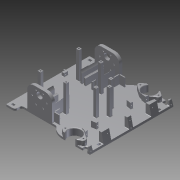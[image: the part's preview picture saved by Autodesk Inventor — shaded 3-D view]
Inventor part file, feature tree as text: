
AUTODESK INVENTOR PART (.ipt)
format: ipt  version: 2011 SP2 (Build 150309200, 309)  size: 1,402,880 bytes
history: native  units: mm
features: extrude x35, sketch x21, projected_geometry x14, fillet x12, mirror x2, plane x1, chamfer x1, hole x1
ambient origin geometry x8: Origin, YZ Plane, XZ Plane, XY Plane, X Axis, Y Axis, Z Axis, Center Point
feature tree (87):
  sketch  "Sketch1"  dims[d0=200.0mm d1=200.0mm]
  extrude  "Extrusion3"  Depth=200.0mm
  extrude  "Extrusion4"  Depth=10.5mm
  extrude  "Extrusion5"  Depth=6.5mm
  extrude  "Extrusion6"  Depth=53.3mm
  extrude  "Extrusion7"  Depth=26.65mm
  sketch  "Sketch4"  dims[d6=6.5mm d8=53.3mm]
  extrude  "Extrusion8"  Depth=5.0mm
  extrude  "Extrusion9"  Depth=5.0mm
  extrude  "Extrusion10"  Depth=4.4mm
  plane  "Work Plane1"
  mirror  "Mirror1"
  sketch  "Sketch9"  dims[d9=53.3mm d10=26.65mm]
  sketch  "Sketch10"  dims[d11=26.65mm d13=5.0mm]
  extrude  "Extrusion16"  Depth=8.0mm
  extrude  "Extrusion17"  Depth=8.0mm
  extrude  "Extrusion18"  Depth=60.0mm
  extrude  "Extrusion19"  Depth=39.0mm
  extrude  "Extrusion20"  Depth=3.65mm
  extrude  "Extrusion21"  Depth=1.5mm
  extrude  "Extrusion22"  Depth=6.6mm
  sketch  "Sketch13"  dims[d18=4.4mm d19=8.0mm]
  extrude  "Extrusion26"  Depth=6.6mm
  extrude  "Extrusion27"  Depth=3.5mm
  extrude  "Extrusion30"  Depth=5.0mm
  extrude  "Extrusion32"  Depth=46.7mm
  extrude  "Extrusion33"  Depth=11.0mm TaperAngle=0.0deg
  extrude  "Extrusion34"  Depth=13.0mm
  chamfer  "Chamfer2"  Distance=38.0mm
  fillet  "Fillet1"  Radius=36.8mm
  extrude  "Extrusion35"  Depth=7.0mm
  extrude  "Extrusion36"  Depth=3.0mm
  sketch  "Sketch21"  dims[d28=1.6mm d29=3.65mm d30=3.65mm]
  extrude  "Extrusion37"  Depth=15.5mm
  extrude  "Extrusion39"  Depth=60.0mm TaperAngle=360.0deg
  extrude  "Extrusion40"  Depth=55.0mm TaperAngle=0.0deg
  fillet  "Fillet2"  Radius=2.0mm
  sketch  "Sketch28"  dims[d44=60.0mm d45=6.6mm]
  extrude  "Extrusion48"  Depth=2.0mm
  extrude  "Extrusion49"  Depth=3.65mm
  extrude  "Extrusion42"  Depth=3.65mm
  extrude  "Extrusion44"  Depth=55.0mm TaperAngle=0.0deg
  fillet  "Fillet4"  Radius=36.8mm
  mirror  "Mirror3"
  fillet  "Fillet3"  Radius=36.0mm
  extrude  "Extrusion45"  Depth=40.0mm TaperAngle=0.0deg
  sketch  "Sketch30"  dims[d49=12.061mm d50=5.0mm]
  extrude  "Extrusion46"  Depth=40.0mm TaperAngle=0.0deg
  extrude  "Extrusion47"  Depth=23.0mm TaperAngle=0.0deg
  hole  "Hole1"  [1 undecoded]
  fillet  "Fillet5"  Radius=6.15mm
  fillet  "Fillet6"  Radius=2.8mm
  fillet  "Fillet7"  Radius=2.8mm
  fillet  "Fillet8"  Radius=2.8mm
  fillet  "Fillet9"  Radius=2.8mm
  fillet  "Fillet10"  Radius=32.757mm
  fillet  "Fillet11"  Radius=32.757mm
  fillet  "Fillet12"  Radius=80.957mm
  extrude  "Extrusion50"  Depth=80.957mm
  extrude  "Extrusion51"  Depth=27.264mm
  sketch  "Sketch2"  dims[d2=10.5mm d3=10.5mm]
  sketch  "Sketch3"  dims[d4=57.861mm d5=6.5mm]
  projected_geometry  "Projected Loop1"
  projected_geometry  "Projected Loop7"
  sketch  "Sketch11"  dims[d14=5.0mm d15=5.0mm]
  sketch  "Sketch12"  dims[d16=6.15mm d17=4.4mm]
  projected_geometry  "Projected Loop8"
  sketch  "Sketch15"  dims[d20=5.0mm d21=8.0mm]
  projected_geometry  "Projected Loop9"
  sketch  "Sketch18"  dims[d22=5.0mm d23=60.0mm]
  projected_geometry  "Projected Loop11"
  sketch  "Sketch20"  dims[d25=138.0mm d27=39.0mm]
  projected_geometry  "Projected Loop12"
  sketch  "Sketch25"  dims[d31=3.0mm d32=0.5mm d34=1.5mm d36=5.0mm]
  sketch  "Sketch27"  dims[d37=3.0mm d38=5.0mm d39=8.15mm d41=6.6mm d42=1.5mm d43=0.5mm]
  projected_geometry  "Projected Loop16"
  sketch  "Sketch29"  dims[d47=11.6mm d48=3.5mm]
  sketch  "Sketch31"  dims[d56=8.15mm d57=46.7mm]
  projected_geometry  "Projected Loop17"
  projected_geometry  "Projected Loop18"
  projected_geometry  "Projected Loop19"
  projected_geometry  "Projected Loop20"
  projected_geometry  "Projected Loop21"
  projected_geometry  "Projected Loop22"
  projected_geometry  "Projected Loop23"
  sketch  "Sketch32"  dims[d58=4.0mm d59=0.0mm d60=11.0mm d61=0.0mm]
  sketch  "Sketch33"  dims[d62=55.0mm d63=0.0mm d64=13.0mm d65=38.0mm d66=36.8mm d67=7.0mm d68=3.0mm d69=15.5mm d70=60.0mm d72=360.0deg d74=55.0mm d75=0.0mm d76=2.0mm d77=2.0mm d78=3.65mm d79=3.65mm d80=55.0mm d81=0.0mm d82=36.8mm d83=36.0mm d84=40.0mm d85=0.0mm d86=40.0mm d87=0.0mm d88=23.0mm d89=0.0mm d90=23.35mm d91=6.15mm d119=2.8mm d120=2.8mm d121=2.8mm d122=2.8mm d135=32.757mm d136=32.757mm d137=80.957mm d138=80.957mm d139=27.264mm d140=20.564mm d141=34.936mm d142=35.936mm d143=2.0mm d144=11.0mm d145=11.0mm d146=2.0mm d147=11.0mm d148=11.0mm d149=2.0mm d150=2.0mm d155=6.0mm d156=6.0mm d157=6.0mm d158=6.0mm d159=3.0mm d160=3.0mm d161=3.0mm d162=3.0mm d163=6.0mm d164=6.0mm d165=3.0mm d166=3.0mm d167=6.0mm d168=6.0mm d169=3.0mm d170=3.0mm d181=3.0mm d182=2.5mm d184=0.0mm d185=0.0mm d186=200.0mm d187=0.0mm d188=200.0mm d189=0.0mm d190=58.0mm d191=0.0mm d192=18.0mm d193=0.0mm d194=40.0mm d195=0.0mm d196=1.570796mm d197=1.570796mm d198=220.0mm d199=220.0mm d200=10.0mm d201=10.0mm d202=5.0mm d203=7.0mm d204=0.0mm d205=0.0mm d215=32.1mm d231=5.0mm d233=12.0mm d234=0.0mm d239=20.0mm d240=0.0mm d256=6.0mm d257=167.0mm d258=6.2mm d259=6.0mm d260=0.0mm d262=22.75mm d266=10.0mm d267=38.9mm d268=5.5mm d269=32.1mm d272=10.0mm d273=12.2mm d276=12.0mm d277=0.0mm d278=28.5mm d279=10.3mm d280=0.0mm d281=5.0mm d282=0.0mm d283=0.5mm d284=5.3mm d285=45.0deg d286=1.0mm d287=5.0mm d288=0.0mm d289=3.0mm d290=3.0mm d291=10.0mm d292=0.0mm d293=6.15mm d294=4.4mm d295=2.0mm d296=3.0mm d297=10.0mm d298=0.0mm d306=41.0mm d307=0.0mm d308=6.0mm d309=6.0mm d310=2.575mm d311=2.575mm d312=2.0mm d313=2.0mm d315=8.956377mm d316=161.0mm d317=10.0mm d318=7.0mm d319=0.0mm d320=32.5mm d335=32.5mm d336=7.0mm d337=12.0mm d338=9.25mm d339=-0.872665mm d343=1.0mm d344=9.25mm d345=-0.872665mm d346=8.0mm d347=4.0mm d348=10.0mm d349=20.0mm d350=0.0mm d351=179.0mm d352=0.0mm d353=179.0mm d354=0.0mm d355=1.5mm d356=3.5mm d357=3.5mm d358=89.5mm d359=89.5mm d360=5.0mm d361=17.5mm d362=2.0mm d363=6.0mm d364=3.0mm d365=2.0mm d366=90.0deg d367=2.0mm d368=3.665191mm d369=6.0mm d370=6.0mm d371=6.0mm d372=6.0mm d373=6.0mm d376=6.0mm d377=2.0mm d378=2.0mm d379=2.0mm d380=3.0mm d382=3.0mm d383=3.0mm d384=3.0mm d386=55.0mm d387=0.0mm d388=40.0mm d389=0.0mm d390=26.0mm d391=69.0mm d392=48.0mm d393=3.0mm d394=13.0mm d395=13.0mm d396=3.0mm d397=1.0mm d398=0.5mm d399=0.5mm d400=1.0mm d401=0.5mm d402=1.0mm d403=15.0mm d404=1.0mm d405=10.0mm d406=0.0mm d407=10.0mm d408=0.0mm]
note: 1 required parameter value undecoded (feature->parameter linkage not recoverable at this tier; creation-order binding heuristic only, values carry confidence <= 0.55)
